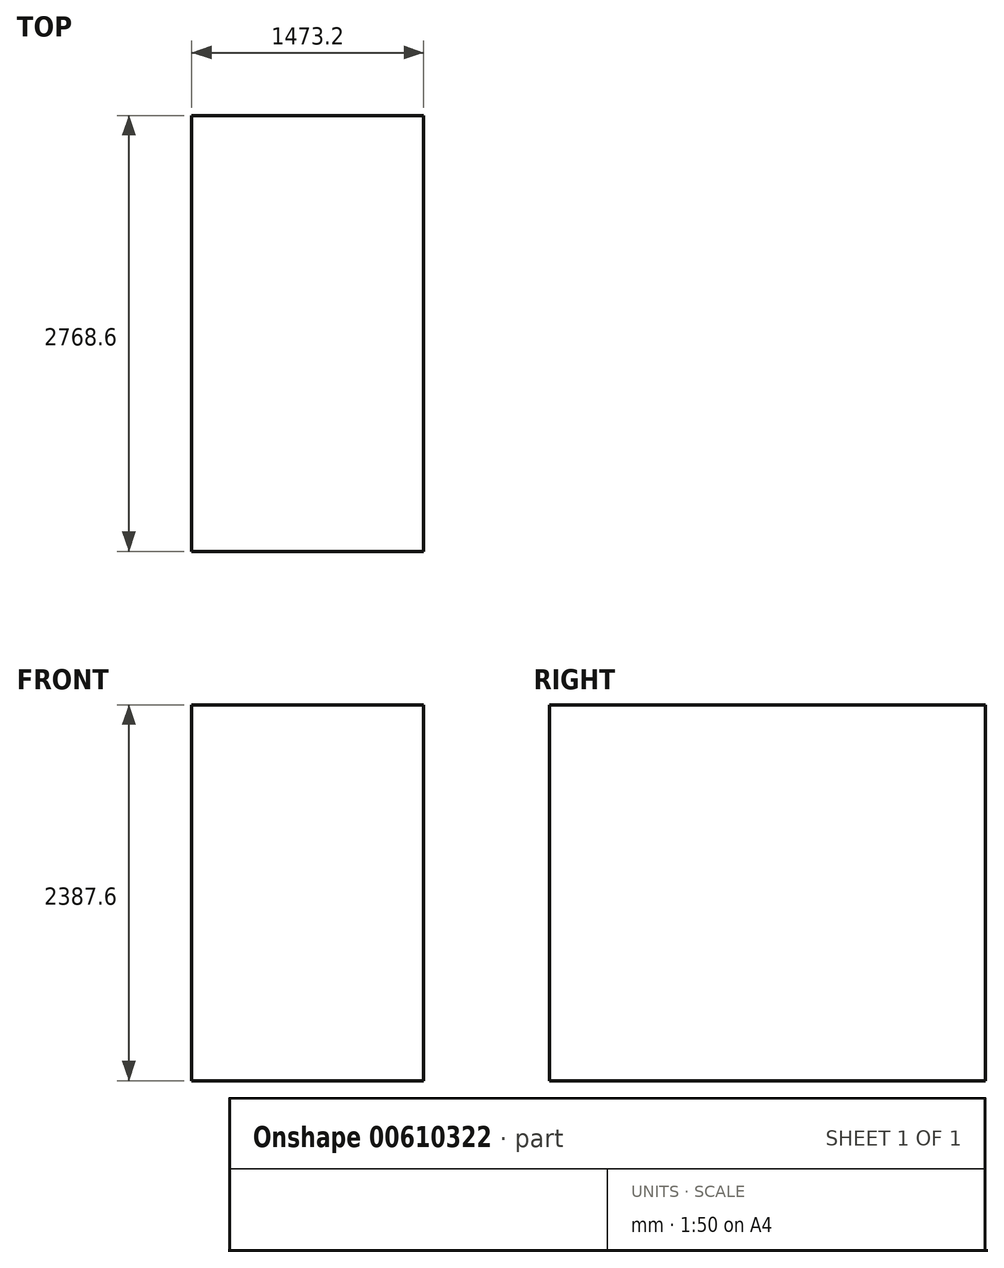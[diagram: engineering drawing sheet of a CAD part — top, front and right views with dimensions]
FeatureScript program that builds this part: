
annotation { "Feature Type Name" : "Feature", "Feature Type Description" : "" }
export const myFeature = defineFeature(function(context is Context, id is Id, definition is map)
    precondition{}
    {
        {
            var Q0;
            Q0=qCreatedBy(makeId("Top.planeOp"),FACE);
            var sketch = newSketch(context, id + "F0", { "sketchPlane" : qUnion([Q0])});
            skLineSegment(sketch, "E0.bottom", {"start": v(-1473.2, 2768.6) * mm, "end": v(0, 2768.6) * mm});
            skLineSegment(sketch, "E0.top", {"start": v(-1473.2, 0) * mm, "end": v(0, 0) * mm});
            skLineSegment(sketch, "E0.left", {"start": v(-1473.2, 2768.6) * mm, "end": v(-1473.2, 0) * mm});
            skLineSegment(sketch, "E0.right", {"start": v(0, 2768.6) * mm, "end": v(0, 0) * mm});
            skSolve(sketch);
        }
        {
            var Q0;
            Q0=makeQuery(id+"F0.imprint","IMPRINT",FACE,{"disambiguationData":[TD([[makeQuery(id+"F0.imprint","IMPRINT",EDGE,{"derivedFrom":sQuery(id+"F0.wireOp",EDGE,"E0.bottom")}),-1.0]])]});
            extrude(context, id + "F1", {"entities" : qUnion([Q0]), "depth" : 2387.6 * mm, "offsetDistance" : 25.4 * mm});
        }
    });
